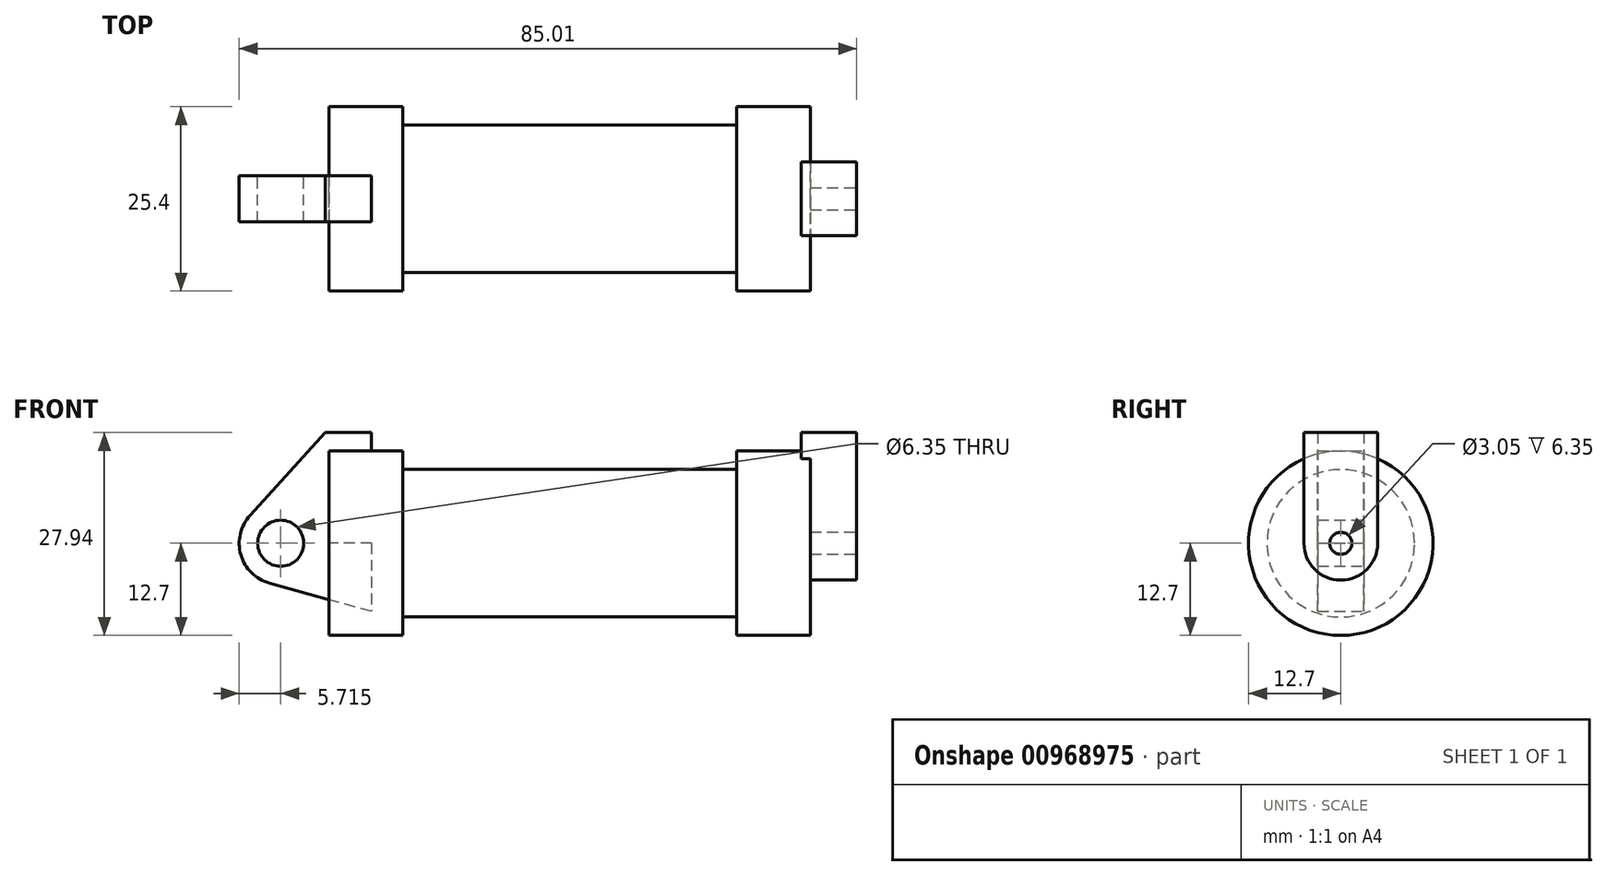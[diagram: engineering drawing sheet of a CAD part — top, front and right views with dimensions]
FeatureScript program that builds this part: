
annotation { "Feature Type Name" : "Feature", "Feature Type Description" : "" }
export const myFeature = defineFeature(function(context is Context, id is Id, definition is map)
    precondition{}
    {
        {
            var Q0;
            Q0=qCreatedBy(makeId("Front.planeOp"),FACE);
            var sketch = newSketch(context, id + "F0", { "sketchPlane" : qUnion([Q0])});
            skLineSegment(sketch, "E0", {"start": v(0, 0) * mm, "end": v(0, 12.7) * mm});
            skLineSegment(sketch, "E1", {"start": v(0, 12.7) * mm, "end": v(10.16, 12.7) * mm});
            skLineSegment(sketch, "E2", {"start": v(10.16, 12.7) * mm, "end": v(10.16, 10.16) * mm});
            skLineSegment(sketch, "E3", {"start": v(10.16, 10.16) * mm, "end": v(56.13, 10.16) * mm});
            skLineSegment(sketch, "E4", {"start": v(56.13, 10.16) * mm, "end": v(56.13, 12.7) * mm});
            skLineSegment(sketch, "E5", {"start": v(56.13, 12.7) * mm, "end": v(66.3, 12.7) * mm});
            skLineSegment(sketch, "E6", {"start": v(66.3, 12.7) * mm, "end": v(66.3, 0) * mm});
            skLineSegment(sketch, "E7", {"start": v(66.3, 0) * mm, "end": v(0, 0) * mm});
            skLineSegment(sketch, "E8", {"start": v(5.84, 15.24) * mm, "end": v(-0.5, 15.24) * mm});
            skLineSegment(sketch, "E9", {"start": v(-0.5, 15.24) * mm, "end": v(-10.88, 3.85) * mm});
            skLineSegment(sketch, "E10", {"start": v(0, 0) * mm, "end": v(-6.65, 0) * mm});
            skCircle(sketch, "E11", {"center": v(-6.65, 0) * mm, "radius": 5.72 * mm});
            skCircle(sketch, "E12", {"center": v(-6.65, 0) * mm, "radius": 3.18 * mm});
            skLineSegment(sketch, "E13", {"start": v(5.84, 15.24) * mm, "end": v(5.84, -9.4) * mm});
            skLineSegment(sketch, "E14", {"start": v(5.84, -9.4) * mm, "end": v(-8.18, -5.5) * mm});
            skSolve(sketch);
        }
        {
            var Q0;
            {var subQ0=sQuery(id+"F0.wireOp",EDGE,"E0");Q0=makeQuery(id+"F0.imprint","IMPRINT",FACE,{"disambiguationData":[TD([[makeQuery(id+"F0.imprint","IMPRINT",EDGE,{"derivedFrom":subQ0}),-1.0]])]});}
            var Q1;
            {var subQ0=sQuery(id+"F0.wireOp",EDGE,"E2");Q1=makeQuery(id+"F0.imprint","IMPRINT",FACE,{"disambiguationData":[TD([[makeQuery(id+"F0.imprint","IMPRINT",EDGE,{"derivedFrom":subQ0}),-1.0]])]});}
            var Q2;
            Q2=sQuery(id+"F0.wireOp",EDGE,"E7");
            revolve(context, id + "F1", {"surfaceOperationType" : NewSurfaceOperationType.NEW, "entities" : qUnion([Q0, Q1]), "axis" : qUnion([Q2]), "revolveType" : RevolveType.ONE_DIRECTION, "angle" : 360 * degree});
        }
        {
            var Q0;
            {var subQ1=sQuery(id+"F0.wireOp",EDGE,"E0");Q0=makeQuery(id+"F0.imprint","IMPRINT",FACE,{"disambiguationData":[TD([[makeQuery(id+"F0.imprint","IMPRINT",EDGE,{"derivedFrom":subQ1}),1.0]])]});}
            var Q1;
            {var subQ5=sQuery(id+"F0.wireOp",EDGE,"E12");Q1=makeQuery(id+"F0.imprint","IMPRINT",FACE,{"disambiguationData":[TD([[makeQuery(id+"F0.imprint","IMPRINT",EDGE,{"derivedFrom":subQ5}),-1.0]])]});}
            var Q2;
            {var subQ0=sQuery(id+"F0.wireOp",EDGE,"E14");Q2=makeQuery(id+"F0.imprint","IMPRINT",FACE,{"disambiguationData":[TD([[makeQuery(id+"F0.imprint","IMPRINT",EDGE,{"derivedFrom":subQ0}),-1.0]])]});}
            extrude(context, id + "F2", {"entities" : qUnion([Q0, Q1, Q2]), "endBound" : BoundingType.SYMMETRIC, "depth" : 6.35 * mm, "offsetDistance" : 25.4 * mm});
        }
        {
            var Q0;
            Q0=makeQuery(id+"F1.opRevolve","SWEPT_FACE",FACE,{"disambiguationData":[OSD([sQuery(id+"F0.wireOp",EDGE,"E6")])]});
            var sketch = newSketch(context, id + "F3", { "sketchPlane" : qUnion([Q0])});
            skCircle(sketch, "E15", {"center": v(0, 0) * mm, "radius": 1.52 * mm});
            skCircle(sketch, "E16", {"center": v(0, 0) * mm, "radius": 5.08 * mm});
            skLineSegment(sketch, "E17", {"start": v(-5.08, 0) * mm, "end": v(-5.08, 15.24) * mm});
            skLineSegment(sketch, "E18", {"start": v(5.08, 0) * mm, "end": v(5.08, 15.24) * mm});
            skLineSegment(sketch, "E19", {"start": v(-5.08, 15.24) * mm, "end": v(5.08, 15.24) * mm});
            skSolve(sketch);
        }
        {
            var Q0;
            Q0=makeQuery(id+"F3.imprint","IMPRINT",FACE,{"disambiguationData":[TD([[makeQuery(id+"F3.imprint","IMPRINT",EDGE,{"derivedFrom":sQuery(id+"F3.wireOp",EDGE,"E15")}),-1.0]])]});
            var Q1;
            {var subQ0=sQuery(id+"F3.wireOp",EDGE,"E17");var subQ1=sQuery(id+"F3.wireOp",EDGE,"E16");var subQ2=makeQuery(id+"F3.imprint","INTERSECT",VERTEX,{"derivedFrom":[subQ1,subQ0]});Q1=makeQuery(id+"F3.imprint","IMPRINT",FACE,{"disambiguationData":[TD([[makeQuery(id+"F3.imprint","IMPRINT",EDGE,{"disambiguationData":[TD([[subQ2,1.0]])],"derivedFrom":subQ1}),-1.0]])]});}
            var Q2;
            {var subQ0=sQuery(id+"F3.wireOp",EDGE,"E19");Q2=makeQuery(id+"F3.imprint","IMPRINT",FACE,{"disambiguationData":[TD([[makeQuery(id+"F3.imprint","IMPRINT",EDGE,{"derivedFrom":subQ0}),-1.0]])]});}
            extrude(context, id + "F4", {"entities" : qUnion([Q0, Q1, Q2]), "operationType" : NewBodyOperationType.ADD, "oppositeDirection" : true, "depth" : 1.27 * mm, "offsetDistance" : 25.4 * mm, "hasSecondDirection" : true, "secondDirectionOppositeDirection" : false, "secondDirectionDepth" : 6.35 * mm});
        }
    });
